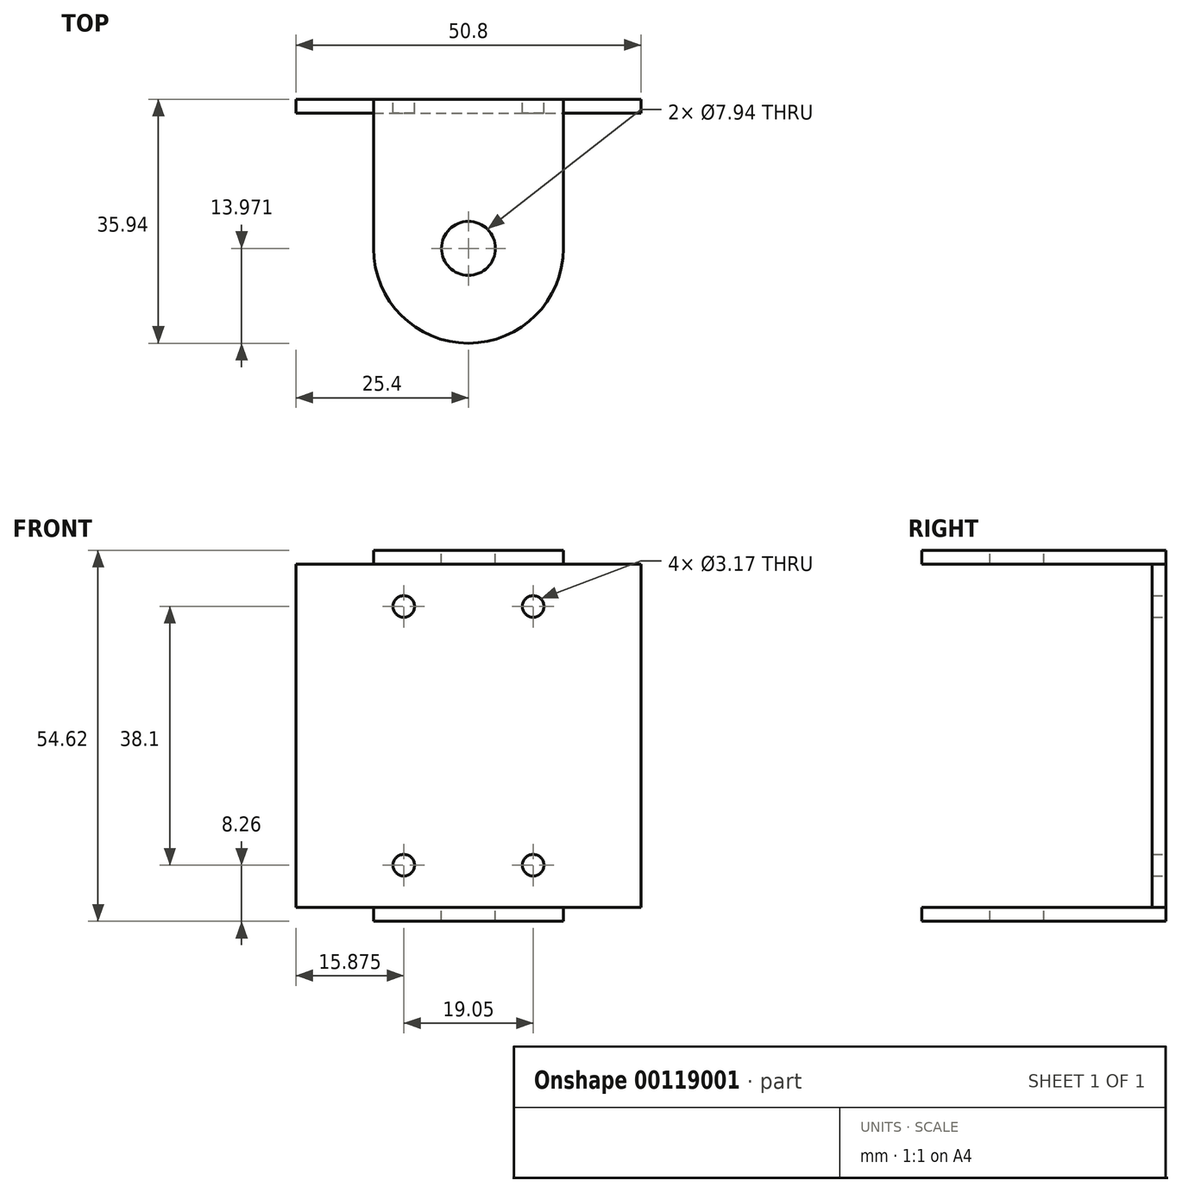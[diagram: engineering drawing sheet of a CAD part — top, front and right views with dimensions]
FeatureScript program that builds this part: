
annotation { "Feature Type Name" : "Feature", "Feature Type Description" : "" }
export const myFeature = defineFeature(function(context is Context, id is Id, definition is map)
    precondition{}
    {
        {
            var Q0;
            Q0=qCreatedBy(makeId("Front.planeOp"),FACE);
            var sketch = newSketch(context, id + "F0", { "sketchPlane" : qUnion([Q0])});
            skLineSegment(sketch, "E0.bottom", {"start": v(-25.4, 27.3) * mm, "end": v(25.4, 27.3) * mm});
            skLineSegment(sketch, "E0.top", {"start": v(-25.4, -27.3) * mm, "end": v(25.4, -27.3) * mm});
            skLineSegment(sketch, "E0.left", {"start": v(-25.4, 27.3) * mm, "end": v(-25.4, -27.3) * mm});
            skLineSegment(sketch, "E0.right", {"start": v(25.4, 27.3) * mm, "end": v(25.4, -27.3) * mm});
            skCircle(sketch, "E1", {"center": v(-9.53, 19.05) * mm, "radius": 1.59 * mm});
            skCircle(sketch, "E2", {"center": v(9.53, 19.05) * mm, "radius": 1.59 * mm});
            skCircle(sketch, "E3", {"center": v(9.53, -19.05) * mm, "radius": 1.59 * mm});
            skCircle(sketch, "E4", {"center": v(-9.53, -19.05) * mm, "radius": 1.59 * mm});
            skSolve(sketch);
        }
        {
            var Q0;
            Q0=makeQuery(id+"F0.imprint","IMPRINT",FACE,{"disambiguationData":[TD([[makeQuery(id+"F0.imprint","IMPRINT",EDGE,{"derivedFrom":sQuery(id+"F0.wireOp",EDGE,"E0.bottom")}),-1.0]])]});
            var Q1;
            Q1=sQuery(id+"F0.wireOp",EDGE,"E1");
            var Q2;
            Q2=sQuery(id+"F0.wireOp",EDGE,"E2");
            var Q3;
            Q3=sQuery(id+"F0.wireOp",EDGE,"E3");
            var Q4;
            Q4=sQuery(id+"F0.wireOp",EDGE,"E4");
            extrude(context, id + "F1", {"entities" : qUnion([Q0]), "surfaceEntities" : qUnion([Q1, Q2, Q3, Q4]), "depth" : 50.8 * mm});
        }
        {
            var Q0;
            Q0=makeQuery(id+"F1.opExtrude","SWEPT_FACE",FACE,{"disambiguationData":[OSD([sQuery(id+"F0.wireOp",EDGE,"E0.bottom")])]});
            var sketch = newSketch(context, id + "F2", { "sketchPlane" : qUnion([Q0])});
            skLineSegment(sketch, "E5.bottom", {"start": v(-25.4, -50.8) * mm, "end": v(25.4, -50.8) * mm});
            skLineSegment(sketch, "E5.top", {"start": v(-25.4, -2.03) * mm, "end": v(-13.97, -2.03) * mm});
            skLineSegment(sketch, "E5.left", {"start": v(-25.4, -50.8) * mm, "end": v(-25.4, -2.03) * mm});
            skLineSegment(sketch, "E5.right", {"start": v(-13.97, -21.97) * mm, "end": v(-13.97, -2.03) * mm});
            skLineSegment(sketch, "E6.top", {"start": v(25.4, -2.03) * mm, "end": v(13.97, -2.03) * mm});
            skLineSegment(sketch, "E6.left", {"start": v(25.4, -50.8) * mm, "end": v(25.4, -2.03) * mm});
            skLineSegment(sketch, "E6.right", {"start": v(13.97, -21.97) * mm, "end": v(13.97, -2.03) * mm});
            skCircle(sketch, "E7", {"center": v(0, -21.97) * mm, "radius": 3.97 * mm});
            skArc(sketch, "E8", {"start": v(-13.97, -21.97) * mm, "mid": v(0, -35.94) * mm, "end": v(13.97, -21.97) * mm});
            skSolve(sketch);
        }
        {
            var Q0;
            Q0 = qSketchRegion(id + "F2", true);
            extrude(context, id + "F3", {"entities" : qUnion([Q0]), "operationType" : NewBodyOperationType.REMOVE, "endBound" : BoundingType.THROUGH_ALL, "oppositeDirection" : true, "depth" : 25.4 * mm});
        }
        {
            var Q0;
            Q0=makeQuery(id+"F3.boolean.opBoolean","COPY",FACE,{"derivedFrom":makeQuery(id+"F3.opExtrude","SWEPT_FACE",FACE,{"disambiguationData":[OSD([sQuery(id+"F2.wireOp",EDGE,"E5.top")])]})});
            var sketch = newSketch(context, id + "F4", { "sketchPlane" : qUnion([Q0])});
            skLineSegment(sketch, "E9.bottom", {"start": v(-25.4, 25.27) * mm, "end": v(25.4, 25.27) * mm});
            skLineSegment(sketch, "E9.top", {"start": v(-25.4, -25.27) * mm, "end": v(25.4, -25.27) * mm});
            skLineSegment(sketch, "E9.left", {"start": v(-25.4, 25.27) * mm, "end": v(-25.4, -25.27) * mm});
            skLineSegment(sketch, "E9.right", {"start": v(25.4, 25.27) * mm, "end": v(25.4, -25.27) * mm});
            skSolve(sketch);
        }
        {
            var Q0;
            Q0 = qSketchRegion(id + "F4", true);
            extrude(context, id + "F5", {"entities" : qUnion([Q0]), "operationType" : NewBodyOperationType.REMOVE, "endBound" : BoundingType.THROUGH_ALL, "depth" : 25.4 * mm});
        }
        {
            var Q0;
            Q0=makeQuery(id+"F5.boolean.opBoolean","MERGE",FACE,{"derivedFrom":[makeQuery(id+"F3.boolean.opBoolean","COPY",FACE,{"derivedFrom":makeQuery(id+"F3.opExtrude","SWEPT_FACE",FACE,{"disambiguationData":[OSD([sQuery(id+"F2.wireOp",EDGE,"E5.top")])]})}),makeQuery(id+"F3.boolean.opBoolean","COPY",FACE,{"derivedFrom":makeQuery(id+"F3.opExtrude","SWEPT_FACE",FACE,{"disambiguationData":[OSD([sQuery(id+"F2.wireOp",EDGE,"E6.top")])]})}),makeQuery(id+"F5.opExtrude","CAP_FACE",FACE,{"disambiguationData":[OSD([sQuery(id+"F4.wireOp",EDGE,"E9.bottom"),sQuery(id+"F4.wireOp",EDGE,"E9.top"),sQuery(id+"F4.wireOp",EDGE,"E9.left"),sQuery(id+"F4.wireOp",EDGE,"E9.right")])],"isStart":true})]});
            var sketch = newSketch(context, id + "F6", { "sketchPlane" : qUnion([Q0])});
            skLineSegment(sketch, "E10.bottom", {"start": v(-25.4, 27.3) * mm, "end": v(-13.97, 27.3) * mm});
            skLineSegment(sketch, "E10.top", {"start": v(-25.4, 25.27) * mm, "end": v(-13.97, 25.27) * mm});
            skLineSegment(sketch, "E10.left", {"start": v(-25.4, 27.3) * mm, "end": v(-25.4, 25.27) * mm});
            skLineSegment(sketch, "E10.right", {"start": v(-13.97, 27.3) * mm, "end": v(-13.97, 25.27) * mm});
            skLineSegment(sketch, "E11.bottom", {"start": v(13.97, 27.3) * mm, "end": v(25.4, 27.3) * mm});
            skLineSegment(sketch, "E11.top", {"start": v(13.97, 25.27) * mm, "end": v(25.4, 25.27) * mm});
            skLineSegment(sketch, "E11.left", {"start": v(13.97, 27.3) * mm, "end": v(13.97, 25.27) * mm});
            skLineSegment(sketch, "E11.right", {"start": v(25.4, 27.3) * mm, "end": v(25.4, 25.27) * mm});
            skLineSegment(sketch, "E12.bottom", {"start": v(13.97, -25.27) * mm, "end": v(25.4, -25.27) * mm});
            skLineSegment(sketch, "E12.top", {"start": v(13.97, -27.3) * mm, "end": v(25.4, -27.3) * mm});
            skLineSegment(sketch, "E12.left", {"start": v(13.97, -25.27) * mm, "end": v(13.97, -27.3) * mm});
            skLineSegment(sketch, "E12.right", {"start": v(25.4, -25.27) * mm, "end": v(25.4, -27.3) * mm});
            skLineSegment(sketch, "E13.bottom", {"start": v(-13.97, -25.27) * mm, "end": v(-25.4, -25.27) * mm});
            skLineSegment(sketch, "E13.top", {"start": v(-13.97, -27.3) * mm, "end": v(-25.4, -27.3) * mm});
            skLineSegment(sketch, "E13.left", {"start": v(-13.97, -25.27) * mm, "end": v(-13.97, -27.3) * mm});
            skLineSegment(sketch, "E13.right", {"start": v(-25.4, -25.27) * mm, "end": v(-25.4, -27.3) * mm});
            skSolve(sketch);
        }
        {
            var Q0;
            Q0 = qSketchRegion(id + "F6", true);
            extrude(context, id + "F7", {"entities" : qUnion([Q0]), "operationType" : NewBodyOperationType.REMOVE, "endBound" : BoundingType.THROUGH_ALL, "oppositeDirection" : true, "depth" : 25.4 * mm});
        }
    });
